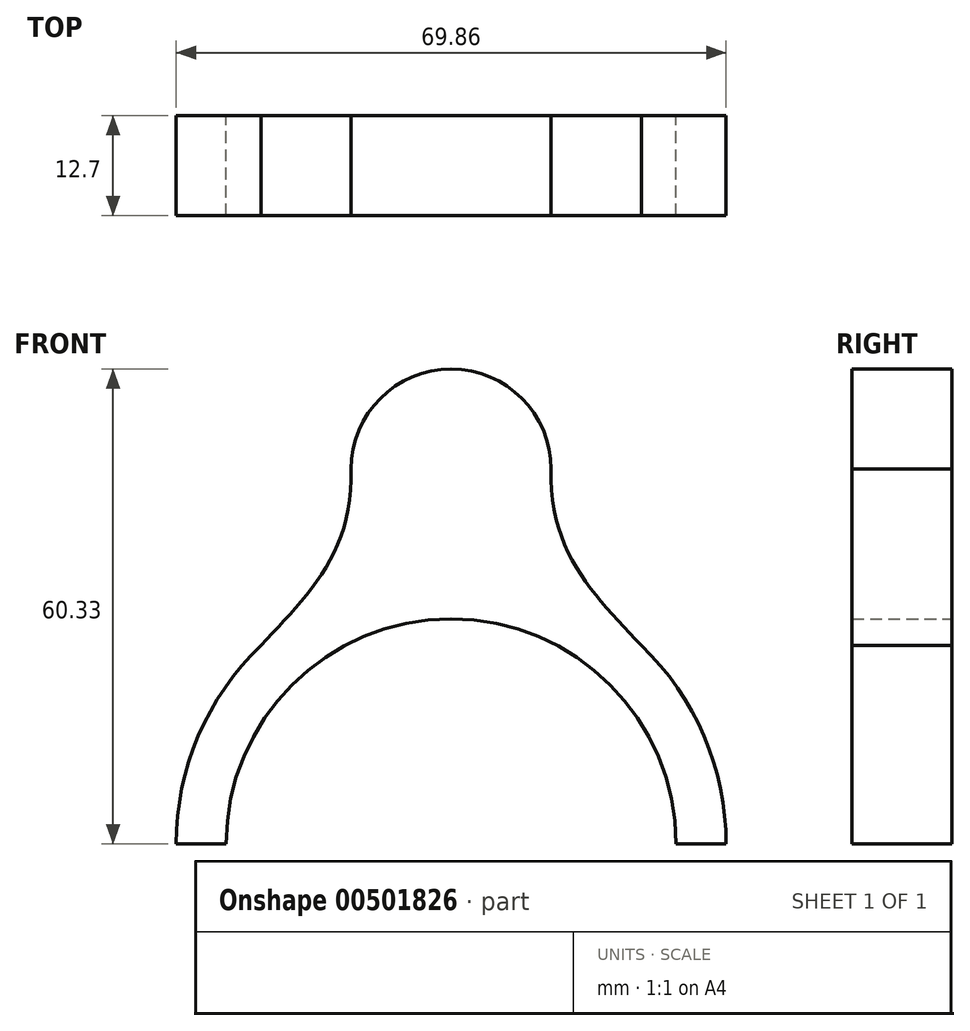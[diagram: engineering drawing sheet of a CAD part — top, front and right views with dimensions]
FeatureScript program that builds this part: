
annotation { "Feature Type Name" : "Feature", "Feature Type Description" : "" }
export const myFeature = defineFeature(function(context is Context, id is Id, definition is map)
    precondition{}
    {
        {
            var Q0;
            Q0=qCreatedBy(makeId("Front.planeOp"),FACE);
            var sketch = newSketch(context, id + "F0", { "sketchPlane" : qUnion([Q0])});
            skArc(sketch, "E0", {"start": v(0, 28.57) * mm, "mid": v(-20.2, 20.2) * mm, "end": v(-28.57, 0) * mm});
            skLineSegment(sketch, "E1", {"start": v(-28.57, 0) * mm, "end": v(-34.93, 0) * mm});
            skLineSegment(sketch, "E2", {"start": v(-34.93, 0) * mm, "end": v(-28.58, 0) * mm});
            skArc(sketch, "E3", {"start": v(0, 60.32) * mm, "mid": v(-8.98, 56.6) * mm, "end": v(-12.7, 47.62) * mm});
            skPoint(sketch, "E4", {"position": v(-30.19, 17.56) * mm});
            skPoint(sketch, "E5", {"position": v(-12.7, 47.62) * mm});
            skFitSpline(sketch, "E6", {"points": [v(-30.19, 17.56) * mm, v(-12.7, 47.62) * mm], "startDerivative": vector(17.49, 30.06) * mm, "endDerivative": vector(-1.43, 44.73) * mm});
            skArc(sketch, "E7.trimOffspring", {"start": v(-24.16, 25.22) * mm, "mid": v(-32.12, 13.71) * mm, "end": v(-34.93, 0) * mm});
            skPoint(sketch, "E8.end.orphan", {"position": v(0, 60.33) * mm});
            skPoint(sketch, "E9.end.orphan", {"position": v(0, 34.93) * mm});
            skLineSegment(sketch, "E10", {"start": v(0, 0) * mm, "end": v(0, 60.32) * mm, "construction": true});
            skLineSegment(sketch, "E11.MirrorCS", {"start": v(28.57, 0) * mm, "end": v(34.93, 0) * mm});
            skArc(sketch, "E12.MirrorCS", {"start": v(0, 60.32) * mm, "mid": v(8.98, 56.6) * mm, "end": v(12.7, 47.62) * mm});
            skLineSegment(sketch, "E13.MirrorCS", {"start": v(34.93, 0) * mm, "end": v(28.58, 0) * mm});
            skArc(sketch, "E14.MirrorCS", {"start": v(0, 28.57) * mm, "mid": v(20.2, 20.2) * mm, "end": v(28.57, 0) * mm});
            skPoint(sketch, "E15.MirrorP", {"position": v(30.19, 17.56) * mm});
            skArc(sketch, "E16.MirrorCS", {"start": v(24.16, 25.22) * mm, "mid": v(32.12, 13.71) * mm, "end": v(34.93, 0) * mm});
            skFitSpline(sketch, "E17.MirrorCS", {"points": [v(30.19, 17.56) * mm, v(12.7, 47.62) * mm], "startDerivative": vector(-17.49, 30.06) * mm, "endDerivative": vector(1.43, 44.73) * mm});
            skSolve(sketch);
        }
        {
            var Q0;
            Q0 = qSketchRegion(id + "F0", true);
            extrude(context, id + "F1", {"entities" : qUnion([Q0]), "depth" : 12.7 * mm});
        }
    });
